# Revit family: AC-C2T-LP
name_source: partatom
category: Communication Devices
revit_build: Autodesk Revit 2017 (Build: 20190508_0315(x64)
units: mm (PartAtom-declared; Revit-internal decimal feet)

## family parameters
Cut with Voids When Loaded = No
Host = Face
Maintain Annotation Orientation = No
Part Type = Normal
Room Calculation Point = No
Round Connector Dimension = Use Diameter
Shared = No

## types (1)
- AC-C2T-LP
    100V Taps = 16, 8, 4, 2 W and 8 Ω bypass
    70V Taps = 16, 8, 4, 2, 1 W and 8 Ω bypass
    Coverage Horizontal = 170.00°
    Coverage Vertical = 170.00°
    Default Elevation = 0 mm
    Depth = 103.4 mm
    Description = Full-range, Ceiling-mount Loudspeaker
    Enclosure Depth = 78 mm
    Enclosure Radius = 114.5 mm
    Grille Depth = 5 mm
    Grille Radius Base = 130 mm
    Grille Radius Extent = 112.5 mm
    Impedance = 8
    Manufacturer = QSC
    Manufacturer URL = www.qsc.com
    Middle Depth = 17 mm
    Middle Radius = 94.5 mm
    Model = AC-C2T-LP
    Product Documentation Link = https://www.qsc.com
    Product Page URL = https://www.qsc.com
    SPL Max = 102
    Sensitivity = 84
    URL = https://www.qsc.com
    Weight Dimensional (kg) = 6.3
    Weight Dimensional (lb) = 13.8
    Weight Product (kg) = 1.9
    Weight Product (lb) = 4.2
    Width = 260 mm
    enclosure material = White Powder Coated Finish

## geometry (parser evidence)
native form markers: Blend x7, Sweep x2
no freeform markers — native parametric forms only
